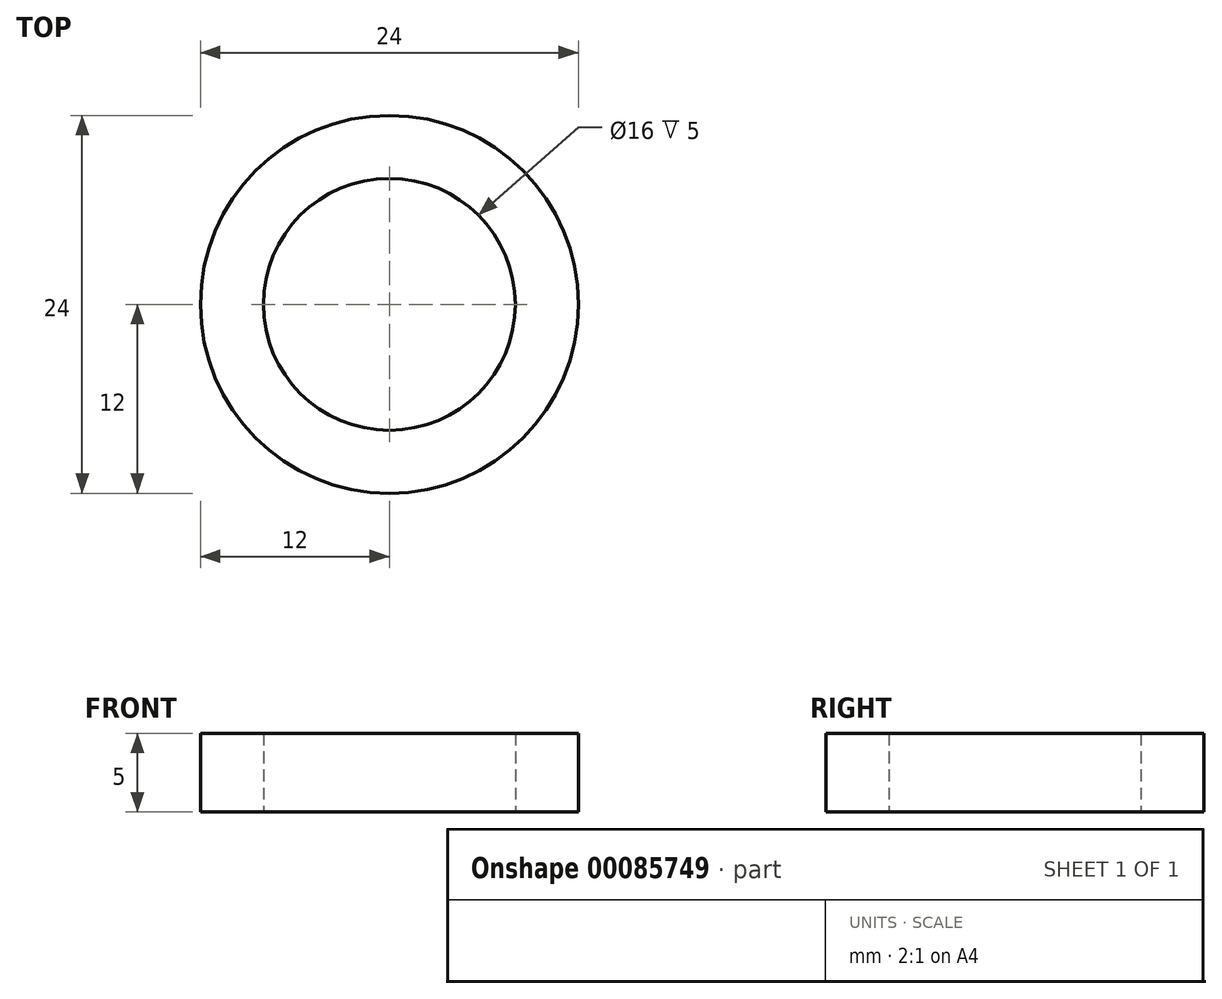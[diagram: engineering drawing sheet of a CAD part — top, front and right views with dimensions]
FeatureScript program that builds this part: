
annotation { "Feature Type Name" : "Feature", "Feature Type Description" : "" }
export const myFeature = defineFeature(function(context is Context, id is Id, definition is map)
    precondition{}
    {
        {
            var Q0;
            Q0=qCreatedBy(makeId("Top.planeOp"),FACE);
            var sketch = newSketch(context, id + "F0", { "sketchPlane" : qUnion([Q0])});
            skCircle(sketch, "E0", {"center": v(0, 0) * mm, "radius": 8 * mm});
            skCircle(sketch, "E1", {"center": v(0, 0) * mm, "radius": 12 * mm});
            skSolve(sketch);
        }
        {
            var Q0;
            Q0=makeQuery(id+"F0.imprint","IMPRINT",FACE,{"disambiguationData":[TD([[makeQuery(id+"F0.imprint","IMPRINT",EDGE,{"derivedFrom":sQuery(id+"F0.wireOp",EDGE,"E0")}),-1.0]])]});
            extrude(context, id + "F1", {"entities" : qUnion([Q0]), "depth" : 5 * mm});
        }
    });
